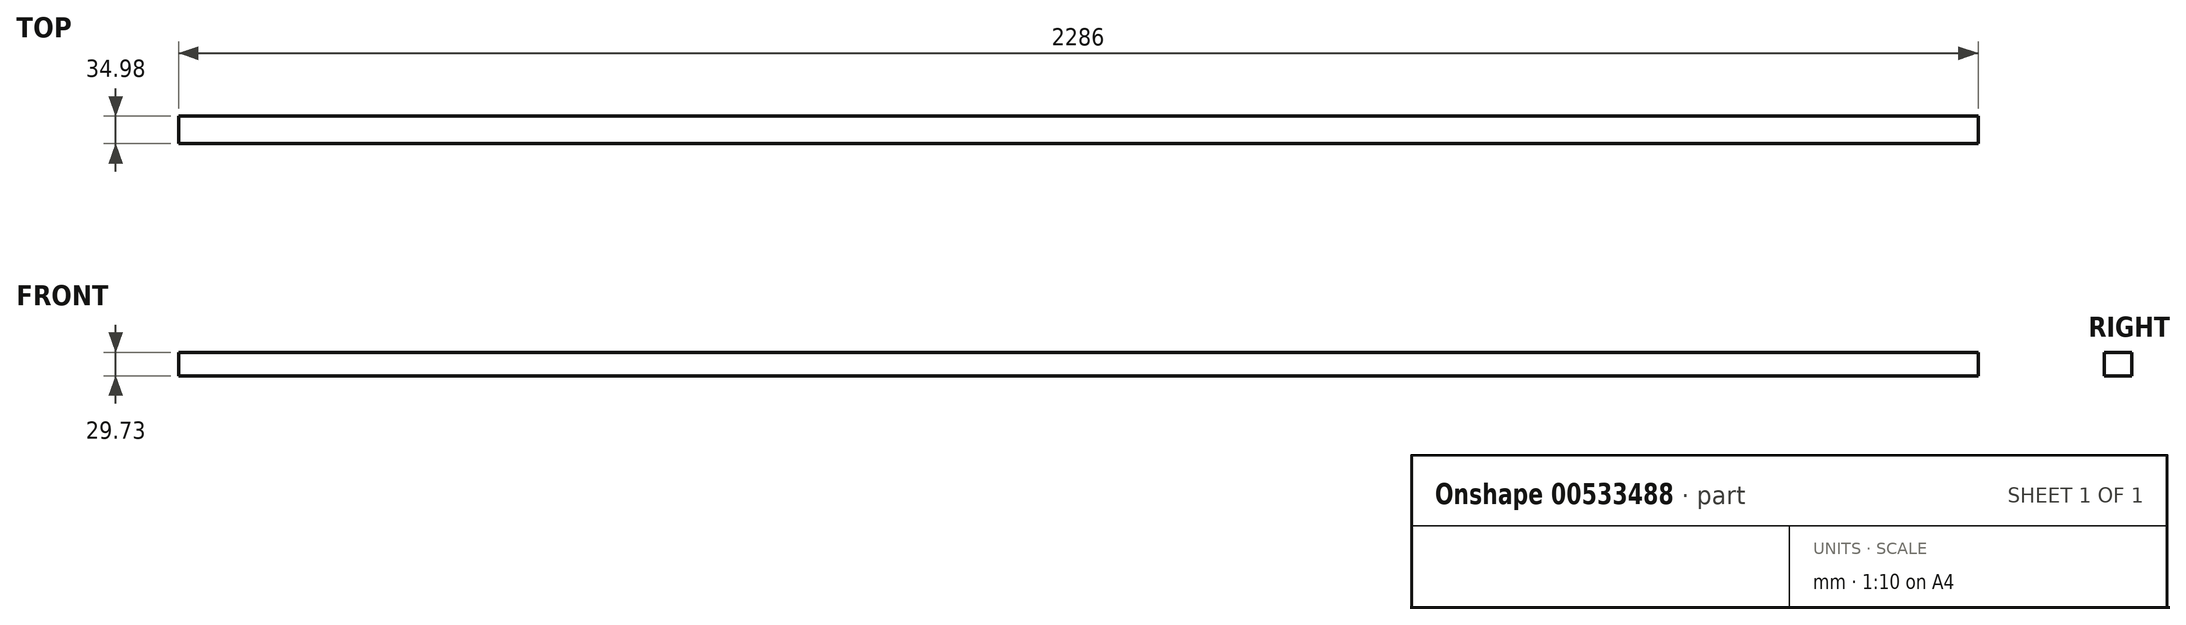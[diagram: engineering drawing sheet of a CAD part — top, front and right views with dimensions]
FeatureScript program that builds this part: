
annotation { "Feature Type Name" : "Feature", "Feature Type Description" : "" }
export const myFeature = defineFeature(function(context is Context, id is Id, definition is map)
    precondition{}
    {
        {
            var Q0;
            Q0=qCreatedBy(makeId("Right.planeOp"),FACE);
            var sketch = newSketch(context, id + "F0", { "sketchPlane" : qUnion([Q0])});
            skLineSegment(sketch, "E0.bottom", {"start": v(23.32, 8.3) * mm, "end": v(-11.66, 8.3) * mm});
            skLineSegment(sketch, "E0.top", {"start": v(23.32, -21.42) * mm, "end": v(-11.66, -21.42) * mm});
            skLineSegment(sketch, "E0.left", {"start": v(23.32, 8.3) * mm, "end": v(23.32, -21.42) * mm});
            skLineSegment(sketch, "E0.right", {"start": v(-11.66, 8.3) * mm, "end": v(-11.66, -21.42) * mm});
            skSolve(sketch);
        }
        {
            var Q0;
            Q0=makeQuery(id+"F0.imprint","IMPRINT",FACE,{"disambiguationData":[TD([[makeQuery(id+"F0.imprint","IMPRINT",EDGE,{"derivedFrom":sQuery(id+"F0.wireOp",EDGE,"E0.bottom")}),1.0]])]});
            extrude(context, id + "F1", {"entities" : qUnion([Q0]), "depth" : 2286 * mm, "offsetDistance" : 25.4 * mm});
        }
    });
